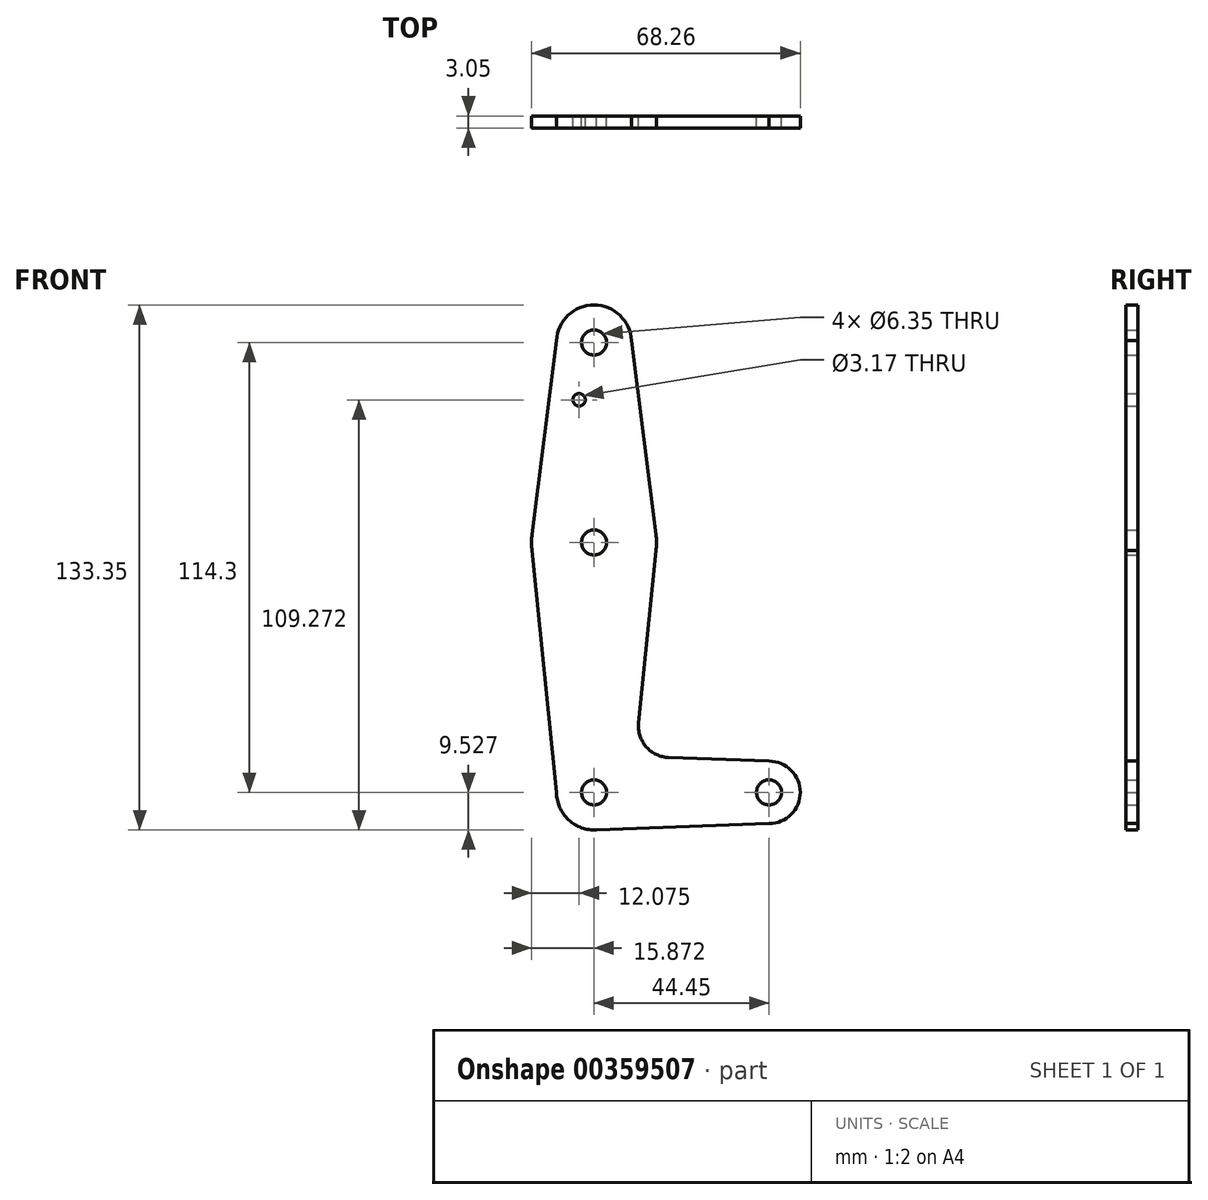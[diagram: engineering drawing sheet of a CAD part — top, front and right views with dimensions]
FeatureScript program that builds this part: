
annotation { "Feature Type Name" : "Feature", "Feature Type Description" : "" }
export const myFeature = defineFeature(function(context is Context, id is Id, definition is map)
    precondition{}
    {
        {
            var Q0;
            Q0=qCreatedBy(makeId("Front.planeOp"),FACE);
            var sketch = newSketch(context, id + "F0", { "sketchPlane" : qUnion([Q0])});
            skCircle(sketch, "E0", {"center": v(-28.68, 62.95) * mm, "radius": 9.53 * mm});
            skCircle(sketch, "E1", {"center": v(-28.68, 12.15) * mm, "radius": 15.88 * mm});
            skCircle(sketch, "E2", {"center": v(-28.68, -51.35) * mm, "radius": 9.53 * mm});
            skCircle(sketch, "E3", {"center": v(15.77, -51.35) * mm, "radius": 7.94 * mm});
            skLineSegment(sketch, "E4", {"start": v(-38.01, 64.83) * mm, "end": v(-44.43, 14.14) * mm});
            skLineSegment(sketch, "E5", {"start": v(-19.34, 64.83) * mm, "end": v(-12.93, 14.14) * mm});
            skLineSegment(sketch, "E6", {"start": v(-12.93, 10.15) * mm, "end": v(-17.34, -33.77) * mm});
            skLineSegment(sketch, "E7", {"start": v(-9.71, -42.5) * mm, "end": v(15.77, -43.42) * mm});
            skCircle(sketch, "E8", {"center": v(-28.68, 12.15) * mm, "radius": 3.18 * mm});
            skCircle(sketch, "E9", {"center": v(-28.68, -51.35) * mm, "radius": 3.18 * mm});
            skCircle(sketch, "E10", {"center": v(15.77, -51.35) * mm, "radius": 3.18 * mm});
            skCircle(sketch, "E11", {"center": v(-28.68, 62.95) * mm, "radius": 3.18 * mm});
            skCircle(sketch, "E12", {"center": v(-32.48, 48.4) * mm, "radius": 1.59 * mm});
            skArc(sketch, "E13.filletArc", {"start": v(-17.34, -33.77) * mm, "mid": v(-15.42, -39.79) * mm, "end": v(-9.71, -42.5) * mm});
            skLineSegment(sketch, "E14", {"start": v(-38.2, -51.35) * mm, "end": v(-44.43, 10.15) * mm});
            skLineSegment(sketch, "E15", {"start": v(-28.68, -60.88) * mm, "end": v(15.77, -59.3) * mm});
            skLineSegment(sketch, "E16", {"start": v(-28.68, -51.35) * mm, "end": v(15.77, -51.35) * mm, "construction": true});
            skLineSegment(sketch, "E17", {"start": v(-28.68, 12.15) * mm, "end": v(-28.68, -51.35) * mm, "construction": true});
            skLineSegment(sketch, "E18", {"start": v(-28.68, 62.95) * mm, "end": v(-28.68, 12.15) * mm, "construction": true});
            skSolve(sketch);
        }
        {
            var Q0;
            Q0 = qSketchRegion(id + "F0", true);
            extrude(context, id + "F1", {"entities" : qUnion([Q0]), "depth" : 3.05 * mm});
        }
    });
